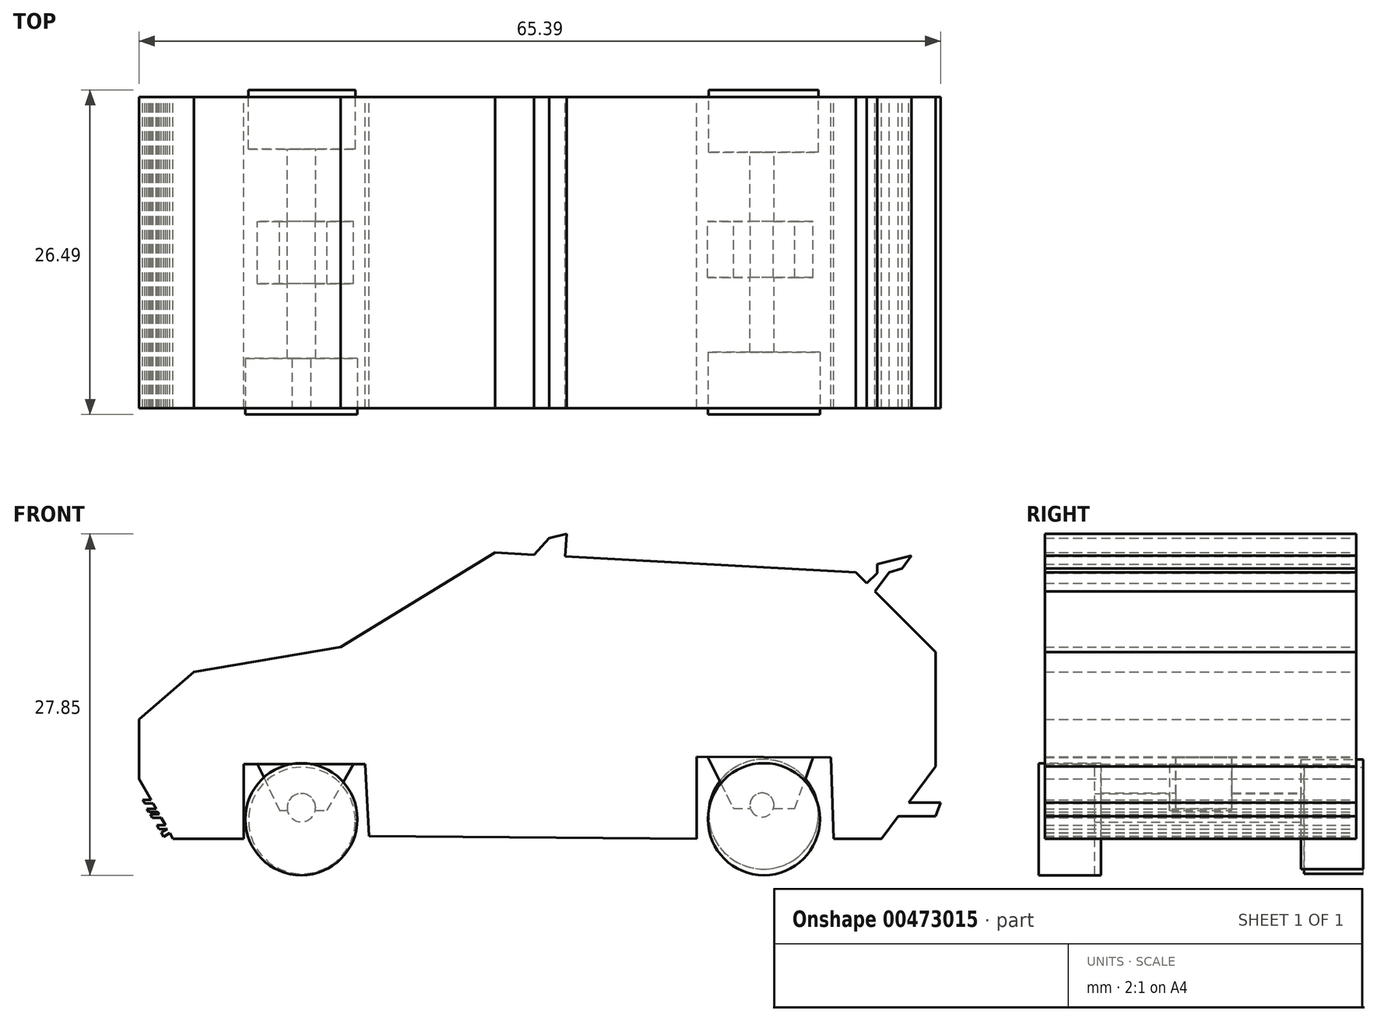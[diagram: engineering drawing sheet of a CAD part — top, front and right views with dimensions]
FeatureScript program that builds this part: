
annotation { "Feature Type Name" : "Feature", "Feature Type Description" : "" }
export const myFeature = defineFeature(function(context is Context, id is Id, definition is map)
    precondition{}
    {
        {
            var Q0;
            Q0=qCreatedBy(makeId("Front.planeOp"),FACE);
            var sketch = newSketch(context, id + "F0", { "sketchPlane" : qUnion([Q0])});
            skLineSegment(sketch, "E0", {"start": v(-36.96, 4.68) * mm, "end": v(-42.74, 4.68) * mm});
            skLineSegment(sketch, "E1", {"start": v(-42.74, 4.68) * mm, "end": v(-45.49, 9.54) * mm});
            skLineSegment(sketch, "E2", {"start": v(-45.49, 9.54) * mm, "end": v(-45.49, 14.42) * mm});
            skLineSegment(sketch, "E3", {"start": v(-45.49, 14.42) * mm, "end": v(-41.02, 18.28) * mm});
            skLineSegment(sketch, "E4", {"start": v(-41.02, 18.28) * mm, "end": v(-29.04, 20.3) * mm});
            skLineSegment(sketch, "E5", {"start": v(-29.04, 20.3) * mm, "end": v(-16.45, 28.02) * mm});
            skLineSegment(sketch, "E6", {"start": v(-16.45, 28.02) * mm, "end": v(13, 26.4) * mm});
            skLineSegment(sketch, "E7", {"start": v(13, 26.4) * mm, "end": v(19.5, 19.9) * mm});
            skLineSegment(sketch, "E8", {"start": v(19.5, 19.9) * mm, "end": v(19.5, 10.56) * mm});
            skLineSegment(sketch, "E9", {"start": v(19.5, 10.56) * mm, "end": v(15.08, 4.68) * mm});
            skLineSegment(sketch, "E10", {"start": v(15.08, 4.68) * mm, "end": v(11.17, 4.68) * mm});
            skLineSegment(sketch, "E11", {"start": v(0, 4.68) * mm, "end": v(-26.75, 4.88) * mm});
            skLineSegment(sketch, "E12", {"start": v(-36.96, 4.68) * mm, "end": v(-36.96, 10.77) * mm});
            skLineSegment(sketch, "E13", {"start": v(-36.96, 10.77) * mm, "end": v(-27.05, 10.77) * mm});
            skLineSegment(sketch, "E14", {"start": v(-27.05, 10.77) * mm, "end": v(-26.75, 4.88) * mm});
            skLineSegment(sketch, "E15", {"start": v(0, 4.68) * mm, "end": v(0, 11.37) * mm});
            skLineSegment(sketch, "E16", {"start": v(0, 11.37) * mm, "end": v(10.97, 11.29) * mm});
            skLineSegment(sketch, "E17", {"start": v(10.97, 11.29) * mm, "end": v(11.17, 4.68) * mm});
            skLineSegment(sketch, "E18", {"start": v(17.29, 7.62) * mm, "end": v(19.9, 7.62) * mm});
            skLineSegment(sketch, "E19", {"start": v(19.9, 7.62) * mm, "end": v(19.5, 6.5) * mm});
            skLineSegment(sketch, "E20", {"start": v(19.5, 6.5) * mm, "end": v(16.44, 6.5) * mm});
            skLineSegment(sketch, "E21", {"start": v(16.44, 6.5) * mm, "end": v(17.29, 7.62) * mm});
            skLineSegment(sketch, "E22", {"start": v(13.88, 25.52) * mm, "end": v(14.72, 26.36) * mm});
            skLineSegment(sketch, "E23", {"start": v(14.72, 26.36) * mm, "end": v(14.72, 27.07) * mm});
            skLineSegment(sketch, "E24", {"start": v(14.72, 27.07) * mm, "end": v(17.54, 27.76) * mm});
            skLineSegment(sketch, "E25", {"start": v(17.54, 27.76) * mm, "end": v(16.77, 26.74) * mm});
            skLineSegment(sketch, "E26", {"start": v(16.77, 26.74) * mm, "end": v(15.73, 26.4) * mm});
            skLineSegment(sketch, "E27", {"start": v(15.73, 26.4) * mm, "end": v(14.55, 24.84) * mm});
            skLineSegment(sketch, "E28", {"start": v(-43.35, 5.77) * mm, "end": v(-44.05, 5.77) * mm});
            skLineSegment(sketch, "E29", {"start": v(-44.05, 5.77) * mm, "end": v(-43.87, 5.45) * mm});
            skLineSegment(sketch, "E30", {"start": v(-43.87, 5.45) * mm, "end": v(-43.17, 5.45) * mm});
            skLineSegment(sketch, "E31", {"start": v(-43.17, 5.45) * mm, "end": v(-43.85, 6.65) * mm});
            skLineSegment(sketch, "E32", {"start": v(-43.85, 6.65) * mm, "end": v(-44.56, 6.65) * mm});
            skLineSegment(sketch, "E33", {"start": v(-44.56, 6.65) * mm, "end": v(-44.41, 6.38) * mm});
            skLineSegment(sketch, "E34", {"start": v(-44.41, 6.38) * mm, "end": v(-43.7, 6.38) * mm});
            skLineSegment(sketch, "E35", {"start": v(-43.7, 6.38) * mm, "end": v(-44.52, 7.83) * mm});
            skLineSegment(sketch, "E36", {"start": v(-44.52, 7.83) * mm, "end": v(-45.2, 7.83) * mm});
            skLineSegment(sketch, "E37", {"start": v(-45.2, 7.83) * mm, "end": v(-45.04, 7.54) * mm});
            skLineSegment(sketch, "E38", {"start": v(-45.04, 7.54) * mm, "end": v(-44.35, 7.54) * mm});
            skLineSegment(sketch, "E39", {"start": v(-44.35, 7.54) * mm, "end": v(-44.11, 7.11) * mm});
            skLineSegment(sketch, "E40", {"start": v(-44.11, 7.11) * mm, "end": v(-44.86, 7.11) * mm});
            skLineSegment(sketch, "E41", {"start": v(-44.86, 7.11) * mm, "end": v(-44.72, 6.85) * mm});
            skLineSegment(sketch, "E42", {"start": v(-44.72, 6.85) * mm, "end": v(-43.96, 6.85) * mm});
            skLineSegment(sketch, "E43", {"start": v(-43.96, 6.85) * mm, "end": v(-43.7, 6.38) * mm});
            skLineSegment(sketch, "E44", {"start": v(-43.7, 6.05) * mm, "end": v(-44.24, 6.05) * mm});
            skPoint(sketch, "E44.startSnap0", {"position": v(-43.51, 6.05) * mm});
            skLineSegment(sketch, "E45", {"start": v(-44.24, 6.05) * mm, "end": v(-44.41, 6.38) * mm});
            skLineSegment(sketch, "E46", {"start": v(-43.17, 5.45) * mm, "end": v(-43.7, 5.15) * mm});
            skLineSegment(sketch, "E47", {"start": v(-43.7, 5.15) * mm, "end": v(-43.51, 4.83) * mm});
            skLineSegment(sketch, "E48", {"start": v(-43.51, 4.83) * mm, "end": v(-42.99, 5.12) * mm});
            skLineSegment(sketch, "E49", {"start": v(-42.99, 5.12) * mm, "end": v(-42.74, 4.68) * mm});
            skLineSegment(sketch, "E50", {"start": v(-13.26, 27.85) * mm, "end": v(-12.02, 29.2) * mm});
            skLineSegment(sketch, "E51", {"start": v(-12.02, 29.2) * mm, "end": v(-10.62, 29.54) * mm});
            skLineSegment(sketch, "E52", {"start": v(-10.62, 29.54) * mm, "end": v(-10.72, 27.7) * mm});
            skLineSegment(sketch, "E53", {"start": v(9.75, 11.3) * mm, "end": v(1.06, 11.36) * mm});
            skSolve(sketch);
        }
        {
            var Q0;
            Q0 = qSketchRegion(id + "F0", true);
            extrude(context, id + "F1", {"entities" : qUnion([Q0]), "depth" : 25.4 * mm});
        }
        {
            var Q0;
            Q0=qCreatedBy(makeId("Front.planeOp"),FACE);
            cPlane(context, id + "F2", {"entities" : qUnion([Q0]), "cplaneType" : CPlaneType.OFFSET, "offset" : 12.7 * mm, "width" : 152.4 * mm, "height" : 152.4 * mm});
        }
        {
            var Q0;
            Q0=qCreatedBy(id+"F2.planeOp",FACE);
            var sketch = newSketch(context, id + "F3", { "sketchPlane" : qUnion([Q0])});
            skLineSegment(sketch, "E54", {"start": v(-35.84, 10.77) * mm, "end": v(-34.04, 6.96) * mm});
            skLineSegment(sketch, "E55", {"start": v(-34.04, 6.96) * mm, "end": v(-30.16, 6.96) * mm});
            skLineSegment(sketch, "E56", {"start": v(-30.16, 6.96) * mm, "end": v(-28, 10.77) * mm});
            skLineSegment(sketch, "E57", {"start": v(-28, 10.77) * mm, "end": v(-35.84, 10.77) * mm});
            skSolve(sketch);
        }
        {
            var Q0;
            Q0 = qSketchRegion(id + "F3", true);
            extrude(context, id + "F4", {"entities" : qUnion([Q0]), "operationType" : NewBodyOperationType.ADD, "depth" : 2.54 * mm, "hasSecondDirection" : true, "secondDirectionOppositeDirection" : true, "secondDirectionDepth" : 2.54 * mm});
        }
        {
            var Q0;
            Q0=qCreatedBy(id+"F2.planeOp",FACE);
            var sketch = newSketch(context, id + "F5", { "sketchPlane" : qUnion([Q0])});
            skSolve(sketch);
        }
        {
            var Q0;
            Q0=qCreatedBy(id+"F2.planeOp",FACE);
            var sketch = newSketch(context, id + "F6", { "sketchPlane" : qUnion([Q0])});
            skLineSegment(sketch, "E58", {"start": v(0.88, 11.37) * mm, "end": v(3, 7.14) * mm});
            skLineSegment(sketch, "E59", {"start": v(7.99, 7.14) * mm, "end": v(9.5, 11.3) * mm});
            skLineSegment(sketch, "E60", {"start": v(9.5, 11.3) * mm, "end": v(0.88, 11.37) * mm});
            skLineSegment(sketch, "E61", {"start": v(3, 7.14) * mm, "end": v(7.99, 7.14) * mm});
            skSolve(sketch);
        }
        {
            var Q0;
            Q0=makeQuery(id+"F6.imprint","IMPRINT",FACE,{"disambiguationData":[TD([[makeQuery(id+"F6.imprint","IMPRINT",EDGE,{"derivedFrom":sQuery(id+"F6.wireOp",EDGE,"E58")}),1.0]])]});
            var Q1;
            Q1 = qSketchRegion(id + "F5", true);
            extrude(context, id + "F7", {"entities" : qUnion([Q0, Q1]), "operationType" : NewBodyOperationType.ADD, "depth" : 2.03 * mm, "hasSecondDirection" : true, "secondDirectionOppositeDirection" : true, "secondDirectionDepth" : 2.54 * mm});
        }
        {
            var Q0;
            Q0=qCreatedBy(id+"F2.planeOp",FACE);
            var sketch = newSketch(context, id + "F8", { "sketchPlane" : qUnion([Q0])});
            skCircle(sketch, "E62", {"center": v(-32.26, 7.2) * mm, "radius": 1.16 * mm});
            skSolve(sketch);
        }
        {
            var Q0;
            Q0 = qSketchRegion(id + "F8", true);
            extrude(context, id + "F9", {"entities" : qUnion([Q0]), "operationType" : NewBodyOperationType.ADD, "depth" : 12.7 * mm, "hasSecondDirection" : true, "secondDirectionOppositeDirection" : true, "secondDirectionDepth" : 12.7 * mm});
        }
        {
            var Q0;
            Q0=qCreatedBy(id+"F2.planeOp",FACE);
            var sketch = newSketch(context, id + "F10", { "sketchPlane" : qUnion([Q0])});
            skCircle(sketch, "E63", {"center": v(5.33, 7.42) * mm, "radius": 0.98 * mm});
            skSolve(sketch);
        }
        {
            var Q0;
            Q0 = qSketchRegion(id + "F10", true);
            extrude(context, id + "F11", {"entities" : qUnion([Q0]), "operationType" : NewBodyOperationType.ADD, "depth" : 12.7 * mm, "hasSecondDirection" : true, "secondDirectionOppositeDirection" : true, "secondDirectionDepth" : 12.7 * mm});
        }
        {
            var Q0;
            Q0=makeQuery(id+"F1.opExtrude","CAP_FACE",FACE,{"disambiguationData":[OSD([sQuery(id+"F0.wireOp",EDGE,"E0"),sQuery(id+"F0.wireOp",EDGE,"E1"),sQuery(id+"F0.wireOp",EDGE,"E2"),sQuery(id+"F0.wireOp",EDGE,"E3"),sQuery(id+"F0.wireOp",EDGE,"E4"),sQuery(id+"F0.wireOp",EDGE,"E5"),sQuery(id+"F0.wireOp",EDGE,"E6"),sQuery(id+"F0.wireOp",EDGE,"E7"),sQuery(id+"F0.wireOp",EDGE,"E8"),sQuery(id+"F0.wireOp",EDGE,"E9"),sQuery(id+"F0.wireOp",EDGE,"E10"),sQuery(id+"F0.wireOp",EDGE,"E11"),sQuery(id+"F0.wireOp",EDGE,"E12"),sQuery(id+"F0.wireOp",EDGE,"E13"),sQuery(id+"F0.wireOp",EDGE,"E14"),sQuery(id+"F0.wireOp",EDGE,"E15"),sQuery(id+"F0.wireOp",EDGE,"E16"),sQuery(id+"F0.wireOp",EDGE,"E17"),sQuery(id+"F0.wireOp",EDGE,"E18"),sQuery(id+"F0.wireOp",EDGE,"E19"),sQuery(id+"F0.wireOp",EDGE,"E20"),sQuery(id+"F0.wireOp",EDGE,"E22"),sQuery(id+"F0.wireOp",EDGE,"E23"),sQuery(id+"F0.wireOp",EDGE,"E24"),sQuery(id+"F0.wireOp",EDGE,"E25"),sQuery(id+"F0.wireOp",EDGE,"E26"),sQuery(id+"F0.wireOp",EDGE,"E27"),sQuery(id+"F0.wireOp",EDGE,"E28"),sQuery(id+"F0.wireOp",EDGE,"E29"),sQuery(id+"F0.wireOp",EDGE,"E30"),sQuery(id+"F0.wireOp",EDGE,"E31"),sQuery(id+"F0.wireOp",EDGE,"E32"),sQuery(id+"F0.wireOp",EDGE,"E33"),sQuery(id+"F0.wireOp",EDGE,"E34"),sQuery(id+"F0.wireOp",EDGE,"E36"),sQuery(id+"F0.wireOp",EDGE,"E37"),sQuery(id+"F0.wireOp",EDGE,"E38"),sQuery(id+"F0.wireOp",EDGE,"E39"),sQuery(id+"F0.wireOp",EDGE,"E40"),sQuery(id+"F0.wireOp",EDGE,"E41"),sQuery(id+"F0.wireOp",EDGE,"E42"),sQuery(id+"F0.wireOp",EDGE,"E43"),sQuery(id+"F0.wireOp",EDGE,"E46"),sQuery(id+"F0.wireOp",EDGE,"E47"),sQuery(id+"F0.wireOp",EDGE,"E48"),sQuery(id+"F0.wireOp",EDGE,"E49"),sQuery(id+"F0.wireOp",EDGE,"E50"),sQuery(id+"F0.wireOp",EDGE,"E51"),sQuery(id+"F0.wireOp",EDGE,"E52"),sQuery(id+"F0.wireOp",EDGE,"E53")])],"isStart":false});
            cPlane(context, id + "F12", {"entities" : qUnion([Q0]), "cplaneType" : CPlaneType.OFFSET, "offset" : 0.5 * mm, "width" : 152.4 * mm, "height" : 152.4 * mm});
        }
        {
            var Q0;
            Q0=qCreatedBy(id+"F12.planeOp",FACE);
            var sketch = newSketch(context, id + "F13", { "sketchPlane" : qUnion([Q0])});
            skCircle(sketch, "E64", {"center": v(-32.26, 6.26) * mm, "radius": 4.57 * mm});
            skSolve(sketch);
        }
        {
            var Q0;
            Q0 = qSketchRegion(id + "F13", true);
            extrude(context, id + "F14", {"entities" : qUnion([Q0]), "operationType" : NewBodyOperationType.ADD, "oppositeDirection" : true, "depth" : 4.57 * mm});
        }
        {
            var Q0;
            Q0=qCreatedBy(id+"F12.planeOp",FACE);
            var sketch = newSketch(context, id + "F15", { "sketchPlane" : qUnion([Q0])});
            skCircle(sketch, "E65", {"center": v(5.48, 6.26) * mm, "radius": 4.57 * mm});
            skPoint(sketch, "E66", {"position": v(-32.26, 6.26) * mm});
            skSolve(sketch);
        }
        {
            var Q0;
            Q0 = qSketchRegion(id + "F15", true);
            extrude(context, id + "F16", {"entities" : qUnion([Q0]), "operationType" : NewBodyOperationType.ADD, "oppositeDirection" : true, "depth" : 5.08 * mm});
        }
        {
            var Q0;
            Q0=qCreatedBy(id+"F12.planeOp",FACE);
            cPlane(context, id + "F17", {"entities" : qUnion([Q0]), "cplaneType" : CPlaneType.OFFSET, "offset" : 26.5 * mm, "oppositeDirection" : true, "width" : 152.4 * mm, "height" : 152.4 * mm});
        }
        {
            var Q0;
            Q0=qCreatedBy(id+"F17.planeOp",FACE);
            var sketch = newSketch(context, id + "F18", { "sketchPlane" : qUnion([Q0])});
            skCircle(sketch, "E67", {"center": v(5.46, 6.67) * mm, "radius": 4.48 * mm});
            skSolve(sketch);
        }
        {
            var Q0;
            Q0 = qSketchRegion(id + "F18", true);
            extrude(context, id + "F19", {"entities" : qUnion([Q0]), "operationType" : NewBodyOperationType.ADD, "depth" : 5.08 * mm});
        }
        {
            var Q0;
            Q0=qCreatedBy(id+"F17.planeOp",FACE);
            var sketch = newSketch(context, id + "F20", { "sketchPlane" : qUnion([Q0])});
            skCircle(sketch, "E68", {"center": v(-32.21, 6.16) * mm, "radius": 4.35 * mm});
            skSolve(sketch);
        }
        {
            var Q0;
            Q0 = qSketchRegion(id + "F20", true);
            extrude(context, id + "F21", {"entities" : qUnion([Q0]), "operationType" : NewBodyOperationType.ADD, "depth" : 4.83 * mm});
        }
        {
            var Q0;
            Q0 = qSketchRegion(id + "F0", true);
            extrude(context, id + "F22", {"entities" : qUnion([Q0]), "depth" : 25.4 * mm});
        }
        {
            var Q0;
            Q0 = qSketchRegion(id + "F0", true);
            extrude(context, id + "F23", {"entities" : qUnion([Q0]), "depth" : 25.4 * mm});
        }
    });
